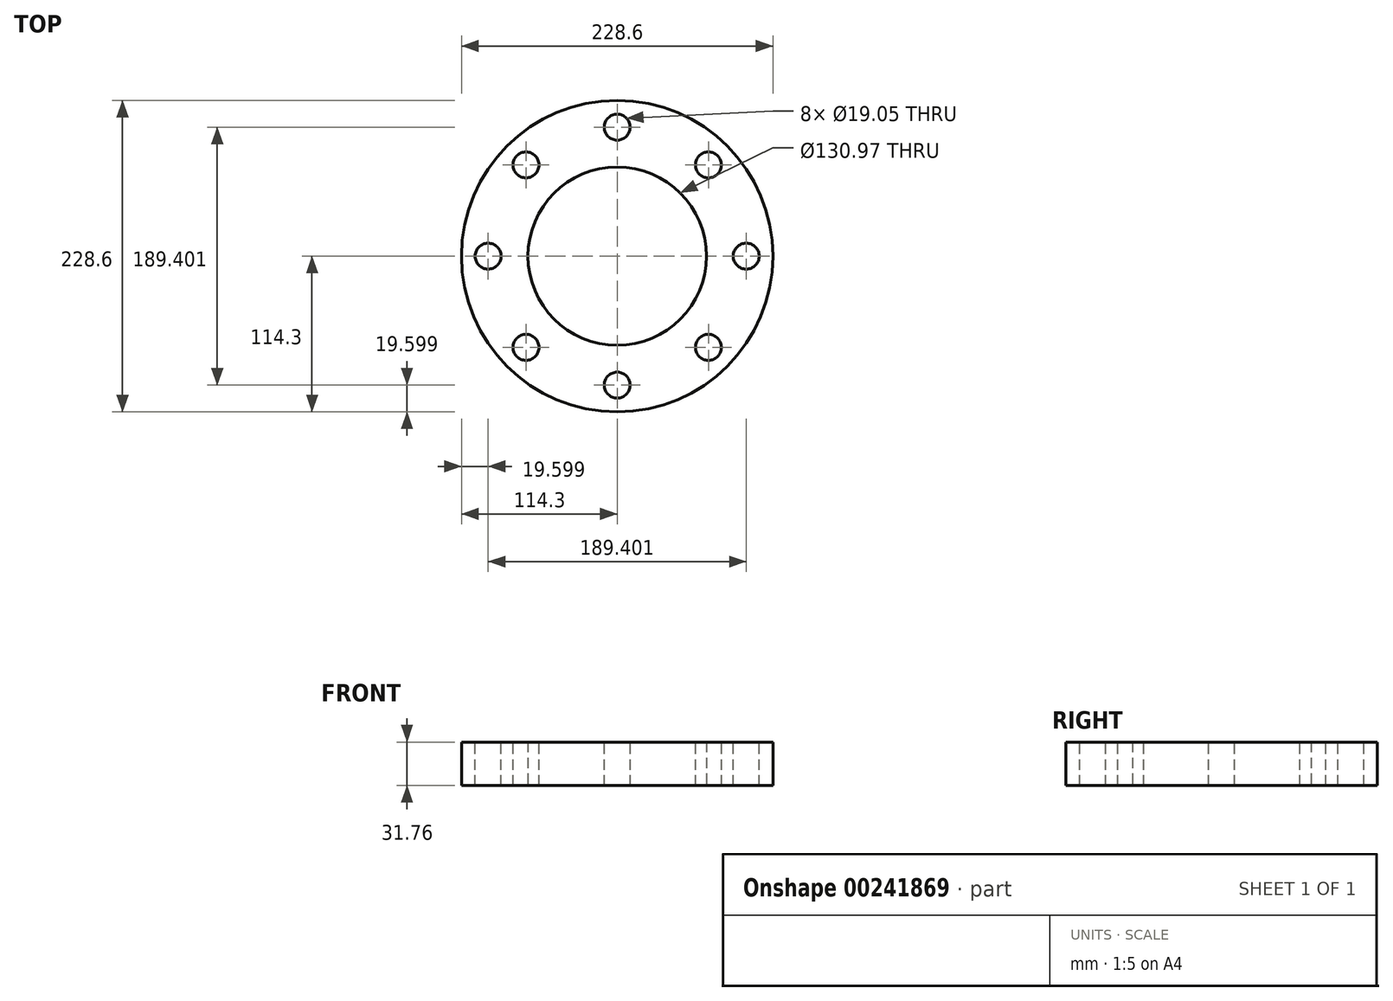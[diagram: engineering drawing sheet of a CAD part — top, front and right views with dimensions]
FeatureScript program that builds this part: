
annotation { "Feature Type Name" : "Feature", "Feature Type Description" : "" }
export const myFeature = defineFeature(function(context is Context, id is Id, definition is map)
    precondition{}
    {
        {
            var Q0;
            Q0=qCreatedBy(makeId("Top.planeOp"),FACE);
            var sketch = newSketch(context, id + "F0", { "sketchPlane" : qUnion([Q0])});
            skCircle(sketch, "E0", {"center": v(0, 0) * mm, "radius": 114.3 * mm});
            skCircle(sketch, "E1", {"center": v(0, 0) * mm, "radius": 65.48 * mm});
            skSolve(sketch);
        }
        {
            var Q0;
            Q0=makeQuery(id+"F0.imprint","IMPRINT",FACE,{"disambiguationData":[TD([[makeQuery(id+"F0.imprint","IMPRINT",EDGE,{"derivedFrom":sQuery(id+"F0.wireOp",EDGE,"E0")}),1.0]])]});
            extrude(context, id + "F1", {"entities" : qUnion([Q0]), "endBound" : BoundingType.SYMMETRIC, "depth" : 31.75 * mm});
        }
        {
            var Q0;
            Q0=makeQuery(id+"F1.opExtrude","CAP_FACE",FACE,{"disambiguationData":[OSD([sQuery(id+"F0.wireOp",EDGE,"E0"),sQuery(id+"F0.wireOp",EDGE,"E1")])],"isStart":false});
            var sketch = newSketch(context, id + "F2", { "sketchPlane" : qUnion([Q0])});
            skLineSegment(sketch, "E2", {"start": v(-240.18, 0) * mm, "end": v(273.96, 0) * mm, "construction": true});
            skCircle(sketch, "E3", {"center": v(0, 94.7) * mm, "radius": 9.53 * mm});
            skCircle(sketch, "E4.1.0", {"center": v(-66.96, 66.96) * mm, "radius": 9.53 * mm});
            skCircle(sketch, "E4.2.0", {"center": v(-94.7, 0) * mm, "radius": 9.53 * mm});
            skCircle(sketch, "E4.3.0", {"center": v(-66.96, -66.96) * mm, "radius": 9.53 * mm});
            skCircle(sketch, "E4.4.0", {"center": v(0, -94.7) * mm, "radius": 9.53 * mm});
            skCircle(sketch, "E4.5.0", {"center": v(66.96, -66.96) * mm, "radius": 9.53 * mm});
            skCircle(sketch, "E4.6.0", {"center": v(94.7, 0) * mm, "radius": 9.53 * mm});
            skCircle(sketch, "E4.7.0", {"center": v(66.96, 66.96) * mm, "radius": 9.53 * mm});
            skPoint(sketch, "E4.center", {"position": v(0, 0) * mm});
            skSolve(sketch);
        }
        {
            var Q0;
            Q0 = qSketchRegion(id + "F2", true);
            extrude(context, id + "F3", {"entities" : qUnion([Q0]), "operationType" : NewBodyOperationType.REMOVE, "endBound" : BoundingType.THROUGH_ALL, "oppositeDirection" : true, "depth" : 25.4 * mm});
        }
    });
